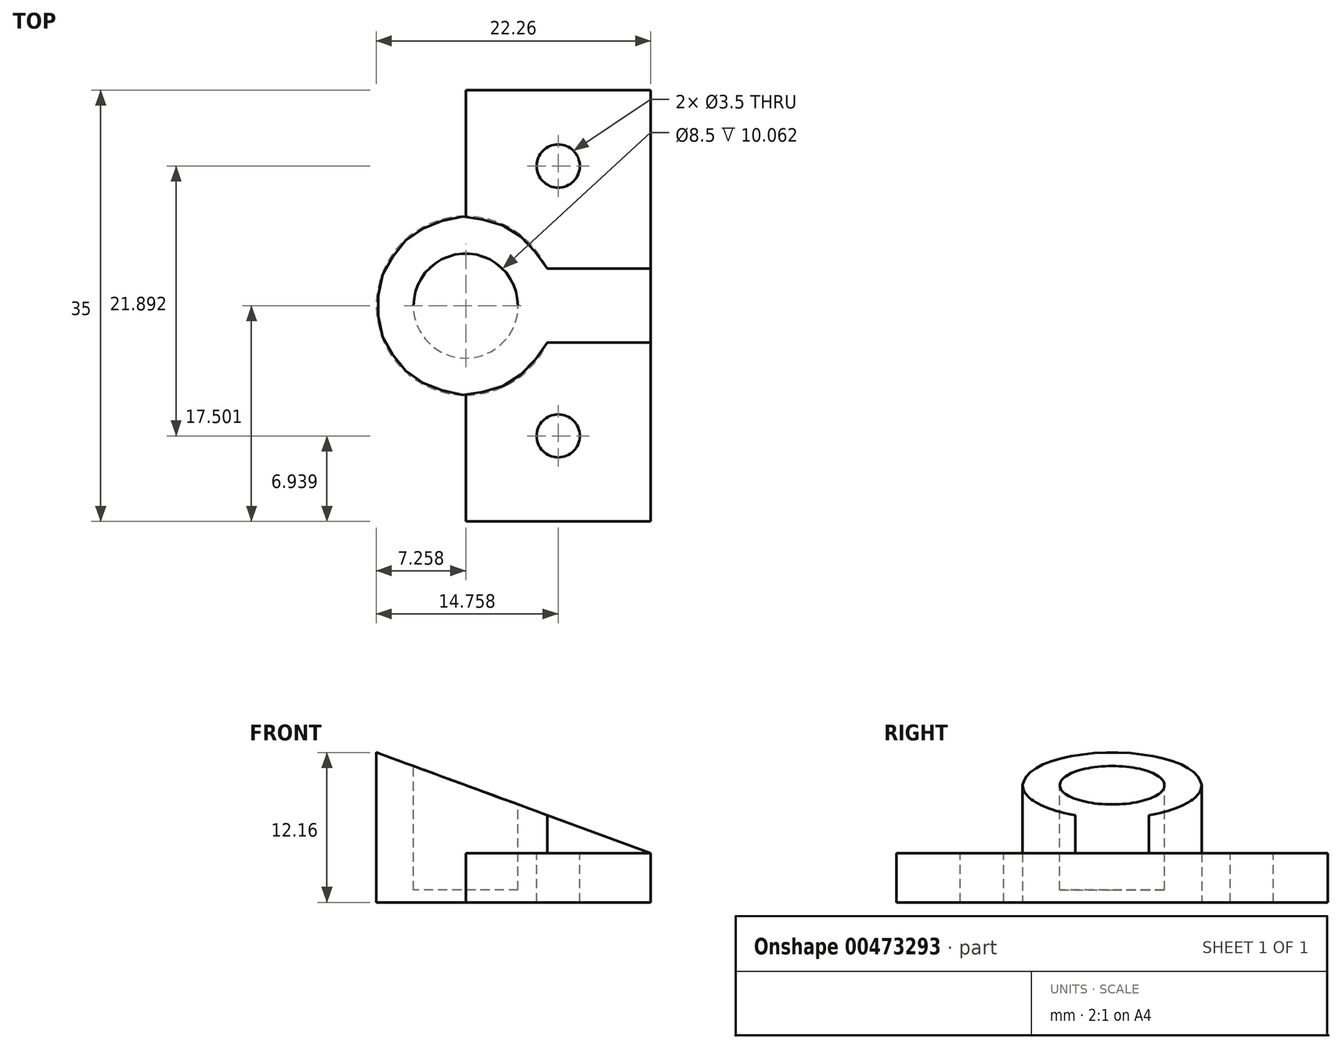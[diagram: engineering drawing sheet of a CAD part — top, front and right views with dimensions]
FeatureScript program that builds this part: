
annotation { "Feature Type Name" : "Feature", "Feature Type Description" : "" }
export const myFeature = defineFeature(function(context is Context, id is Id, definition is map)
    precondition{}
    {
        {
            var Q0;
            Q0=qCreatedBy(makeId("Top.planeOp"),FACE);
            var sketch = newSketch(context, id + "F0", { "sketchPlane" : qUnion([Q0])});
            skLineSegment(sketch, "E0.bottom", {"start": v(15.73, -2.25) * mm, "end": v(0.73, -2.25) * mm});
            skLineSegment(sketch, "E0.top", {"start": v(15.73, 32.75) * mm, "end": v(0.73, 32.75) * mm});
            skLineSegment(sketch, "E0.left", {"start": v(15.73, -2.25) * mm, "end": v(15.73, 32.75) * mm});
            skLineSegment(sketch, "E0.right", {"start": v(0.73, -2.25) * mm, "end": v(0.73, 32.75) * mm});
            skSolve(sketch);
        }
        {
            var Q0;
            Q0=qSketchRegion(id+"F0",true);
            extrude(context, id + "F1", {"entities" : qUnion([Q0]), "depth" : 4 * mm, "offsetDistance" : 25 * mm});
        }
        {
            var Q0;
            Q0=makeQuery(id+"F1.opExtrude","SWEPT_FACE",FACE,{"disambiguationData":[OSD([sQuery(id+"F0.wireOp",EDGE,"E0.top")])]});
            var sketch = newSketch(context, id + "F2", { "sketchPlane" : qUnion([Q0])});
            skArc(sketch, "E1", {"start": v(23.96, 8.4) * mm, "mid": v(24.64, 14.63) * mm, "end": v(18.7, 16.63) * mm});
            skCircle(sketch, "E2", {"center": v(20.42, 11.94) * mm, "radius": 1.75 * mm});
            skLineSegment(sketch, "E3", {"start": v(23.96, 8.4) * mm, "end": v(15.56, 0) * mm});
            skLineSegment(sketch, "E4", {"start": v(-0.73, 0) * mm, "end": v(15.56, 0) * mm});
            skLineSegment(sketch, "E5", {"start": v(-15.73, 4) * mm, "end": v(-0.73, 4) * mm});
            skLineSegment(sketch, "E6", {"start": v(-0.73, 4) * mm, "end": v(-0.73, 0) * mm});
            skLineSegment(sketch, "E7", {"start": v(-15.73, 4) * mm, "end": v(18.7, 16.63) * mm});
            skSolve(sketch);
        }
        {
            var Q0;
            Q0=qSketchRegion(id+"F2",true);
            extrude(context, id + "F3", {"entities" : qUnion([Q0]), "operationType" : NewBodyOperationType.ADD, "oppositeDirection" : true, "depth" : 35 * mm, "offsetDistance" : 25 * mm});
        }
        {
            var Q0;
            Q0=makeQuery(id+"F1.opExtrude","SWEPT_FACE",FACE,{"disambiguationData":[OSD([sQuery(id+"F0.wireOp",EDGE,"E0.left")])]});
            var sketch = newSketch(context, id + "F4", { "sketchPlane" : qUnion([Q0])});
            skLineSegment(sketch, "E8.bottom", {"start": v(3.25, 4) * mm, "end": v(12.25, 4) * mm});
            skLineSegment(sketch, "E8.top", {"start": v(3.25, 18.37) * mm, "end": v(12.25, 18.37) * mm});
            skLineSegment(sketch, "E8.left", {"start": v(3.25, 4) * mm, "end": v(3.25, 18.37) * mm});
            skLineSegment(sketch, "E8.right", {"start": v(12.25, 4) * mm, "end": v(12.25, 18.37) * mm});
            skLineSegment(sketch, "E9.bottom", {"start": v(18.25, 4) * mm, "end": v(27.25, 4) * mm});
            skLineSegment(sketch, "E9.top", {"start": v(18.25, 18.22) * mm, "end": v(27.25, 18.22) * mm});
            skLineSegment(sketch, "E9.left", {"start": v(18.25, 4) * mm, "end": v(18.25, 18.22) * mm});
            skLineSegment(sketch, "E9.right", {"start": v(27.25, 4) * mm, "end": v(27.25, 18.22) * mm});
            skSolve(sketch);
        }
        {
            var Q0;
            Q0=qSketchRegion(id+"F4",true);
            extrude(context, id + "F5", {"entities" : qUnion([Q0]), "operationType" : NewBodyOperationType.REMOVE, "oppositeDirection" : true, "depth" : 47.1 * mm, "offsetDistance" : 25 * mm});
        }
        {
            var Q0;
            Q0=makeQuery(id+"F5.boolean.opBoolean","COPY",FACE,{"derivedFrom":makeQuery(id+"F5.opExtrude","SWEPT_FACE",FACE,{"disambiguationData":[OSD([sQuery(id+"F4.wireOp",EDGE,"E9.bottom")])]})});
            var sketch = newSketch(context, id + "F6", { "sketchPlane" : qUnion([Q0])});
            skPoint(sketch, "E10.0", {"position": v(15.73, 15.25) * mm});
            skCircle(sketch, "E11", {"center": v(0.73, 15.25) * mm, "radius": 4.25 * mm});
            skCircle(sketch, "E12", {"center": v(0.73, 15.25) * mm, "radius": 8 * mm, "construction": true});
            skSolve(sketch);
        }
        {
            var Q0;
            Q0=qSketchRegion(id+"F6",true);
            extrude(context, id + "F7", {"entities" : qUnion([Q0]), "operationType" : NewBodyOperationType.REMOVE, "oppositeDirection" : true, "depth" : 3 * mm, "offsetDistance" : 25 * mm, "hasSecondDirection" : true, "secondDirectionOppositeDirection" : false, "secondDirectionDepth" : 83.2 * mm});
        }
        {
            var Q0;
            Q0=makeQuery(id+"F5.boolean.opBoolean","COPY",FACE,{"derivedFrom":makeQuery(id+"F5.opExtrude","SWEPT_FACE",FACE,{"disambiguationData":[OSD([sQuery(id+"F4.wireOp",EDGE,"E9.bottom")])]})});
            var sketch = newSketch(context, id + "F8", { "sketchPlane" : qUnion([Q0])});
            skCircle(sketch, "E13", {"center": v(0.73, 15.25) * mm, "radius": 7.26 * mm});
            skArc(sketch, "E14.0", {"start": v(-2.28, 18.25) * mm, "mid": v(0.73, 19.5) * mm, "end": v(3.74, 18.25) * mm});
            skCircle(sketch, "E15.0.0", {"center": v(0.73, 15.25) * mm, "radius": 4.25 * mm});
            skSolve(sketch);
        }
        {
            var Q0;
            Q0=qSketchRegion(id+"F8",true);
            var Q1;
            {var subQ0=makeQuery(id+"F3.opExtrude","SWEPT_FACE",FACE,{"disambiguationData":[OSD([sQuery(id+"F2.wireOp",EDGE,"E1")])]});var subQ1=makeQuery(id+"F5.opExtrude","SWEPT_FACE",FACE,{"disambiguationData":[OSD([sQuery(id+"F4.wireOp",EDGE,"E8.right")])]});Q1=makeQuery(id+"F7.boolean.opBoolean","SPLIT",FACE,{"disambiguationData":[TD([subQ0])],"derivedFrom":makeQuery(id+"F5.boolean.opBoolean","SPLIT",FACE,{"disambiguationData":[TD([subQ1])],"derivedFrom":makeQuery(id+"F3.opExtrude","SWEPT_FACE",FACE,{"disambiguationData":[OSD([sQuery(id+"F2.wireOp",EDGE,"E7")])]})})});}
            extrude(context, id + "F9", {"entities" : qUnion([Q0]), "operationType" : NewBodyOperationType.ADD, "endBound" : BoundingType.UP_TO_SURFACE, "depth" : 25 * mm, "endBoundEntityFace" : qUnion([Q1]), "offsetDistance" : 25 * mm});
        }
        {
            var Q0;
            Q0=makeQuery(id+"F3.boolean.opBoolean","MERGE",FACE,{"derivedFrom":[makeQuery(id+"F1.opExtrude","CAP_FACE",FACE,{"disambiguationData":[OSD([sQuery(id+"F0.wireOp",EDGE,"E0.bottom"),sQuery(id+"F0.wireOp",EDGE,"E0.top"),sQuery(id+"F0.wireOp",EDGE,"E0.left"),sQuery(id+"F0.wireOp",EDGE,"E0.right")])],"isStart":true}),makeQuery(id+"F3.opExtrude","SWEPT_FACE",FACE,{"disambiguationData":[OSD([sQuery(id+"F2.wireOp",EDGE,"E4")])]})]});
            var sketch = newSketch(context, id + "F10", { "sketchPlane" : qUnion([Q0])});
            skPoint(sketch, "E16", {"position": v(0.73, 2.25) * mm});
            skLineSegment(sketch, "E17.0", {"start": v(-19.56, -3.25) * mm, "end": v(-19.56, -12.25) * mm});
            skLineSegment(sketch, "E18.0", {"start": v(-19.56, -18.25) * mm, "end": v(-19.56, -27.25) * mm});
            skLineSegment(sketch, "E19.bottom", {"start": v(-19.56, -3.25) * mm, "end": v(0.73, -3.25) * mm});
            skLineSegment(sketch, "E19.top", {"start": v(-19.56, -12.25) * mm, "end": v(-5.88, -12.25) * mm});
            skLineSegment(sketch, "E19.right", {"start": v(0.73, -3.25) * mm, "end": v(0.73, -8) * mm});
            skLineSegment(sketch, "E20.bottom", {"start": v(-19.56, -18.25) * mm, "end": v(-5.88, -18.25) * mm});
            skLineSegment(sketch, "E20.top", {"start": v(-19.56, -27.25) * mm, "end": v(0.73, -27.25) * mm});
            skLineSegment(sketch, "E20.right", {"start": v(0.73, -22.5) * mm, "end": v(0.73, -27.25) * mm});
            skArc(sketch, "E21.0", {"start": v(0.73, -22.5) * mm, "mid": v(-3.2, -21.35) * mm, "end": v(-5.88, -18.25) * mm});
            skArc(sketch, "E22.0", {"start": v(-5.88, -12.25) * mm, "mid": v(-3.2, -9.15) * mm, "end": v(0.73, -8) * mm});
            skPoint(sketch, "E23.orphan", {"position": v(7.34, -18.25) * mm});
            skPoint(sketch, "E24.orphan", {"position": v(0.73, -12.25) * mm});
            skPoint(sketch, "E25.orphan", {"position": v(7.34, -12.25) * mm});
            skSolve(sketch);
        }
        {
            var Q0;
            Q0=qSketchRegion(id+"F10",true);
            extrude(context, id + "F11", {"entities" : qUnion([Q0]), "operationType" : NewBodyOperationType.REMOVE, "oppositeDirection" : true, "depth" : 25 * mm, "offsetDistance" : 25 * mm});
        }
        {
            var Q0;
            Q0=makeQuery(id+"F5.boolean.opBoolean","COPY",FACE,{"derivedFrom":makeQuery(id+"F5.opExtrude","SWEPT_FACE",FACE,{"disambiguationData":[OSD([sQuery(id+"F4.wireOp",EDGE,"E8.bottom")])]})});
            var sketch = newSketch(context, id + "F12", { "sketchPlane" : qUnion([Q0])});
            skCircle(sketch, "E26", {"center": v(8.23, 4.69) * mm, "radius": 1.75 * mm});
            skPoint(sketch, "E26.centerSnap0", {"position": v(15.73, 7.75) * mm});
            skPoint(sketch, "E26.centerSnap1", {"position": v(8.23, 3.25) * mm});
            skPoint(sketch, "E27.0", {"position": v(15.73, 22.75) * mm});
            skCircle(sketch, "E28", {"center": v(8.23, 26.58) * mm, "radius": 1.75 * mm});
            skSolve(sketch);
        }
        {
            var Q0;
            Q0=qSketchRegion(id+"F12",true);
            extrude(context, id + "F13", {"entities" : qUnion([Q0]), "operationType" : NewBodyOperationType.REMOVE, "oppositeDirection" : true, "depth" : 25 * mm, "offsetDistance" : 25 * mm});
        }
        {
            var Q0;
            Q0=makeQuery(id+"F11.boolean.opBoolean","MERGE",FACE,{"derivedFrom":[makeQuery(id+"F5.boolean.opBoolean","COPY",FACE,{"derivedFrom":makeQuery(id+"F5.opExtrude","SWEPT_FACE",FACE,{"disambiguationData":[OSD([sQuery(id+"F4.wireOp",EDGE,"E9.right")])]})})],"fromTools":[makeQuery(id+"F11.opExtrude","SWEPT_FACE",FACE,{"disambiguationData":[OSD([sQuery(id+"F10.wireOp",EDGE,"E20.top")])]})]});
            extrude(context, id + "F14", {"entities" : qUnion([Q0]), "operationType" : NewBodyOperationType.REMOVE, "oppositeDirection" : true, "depth" : 25 * mm, "offsetDistance" : 25 * mm});
        }
        {
            var Q0;
            Q0=makeQuery(id+"F11.boolean.opBoolean","MERGE",FACE,{"derivedFrom":[makeQuery(id+"F5.boolean.opBoolean","COPY",FACE,{"derivedFrom":makeQuery(id+"F5.opExtrude","SWEPT_FACE",FACE,{"disambiguationData":[OSD([sQuery(id+"F4.wireOp",EDGE,"E8.left")])]})})],"fromTools":[makeQuery(id+"F11.opExtrude","SWEPT_FACE",FACE,{"disambiguationData":[OSD([sQuery(id+"F10.wireOp",EDGE,"E19.bottom")])]})]});
            extrude(context, id + "F15", {"entities" : qUnion([Q0]), "operationType" : NewBodyOperationType.REMOVE, "oppositeDirection" : true, "depth" : 25 * mm, "offsetDistance" : 25 * mm});
        }
        {
            var Q0;
            Q0=makeQuery(id+"F11.boolean.opBoolean","MERGE",FACE,{"derivedFrom":[makeQuery(id+"F7.boolean.opBoolean","SPLIT",FACE,{"disambiguationData":[TD([makeQuery(id+"F3.opExtrude","SWEPT_FACE",FACE,{"disambiguationData":[OSD([sQuery(id+"F2.wireOp",EDGE,"E1")])]})])],"derivedFrom":makeQuery(id+"F5.boolean.opBoolean","COPY",FACE,{"derivedFrom":makeQuery(id+"F5.opExtrude","SWEPT_FACE",FACE,{"disambiguationData":[OSD([sQuery(id+"F4.wireOp",EDGE,"E8.right")])]})})})],"fromTools":[makeQuery(id+"F11.opExtrude","SWEPT_FACE",FACE,{"disambiguationData":[OSD([sQuery(id+"F10.wireOp",EDGE,"E19.top")])]})]});
            extrude(context, id + "F16", {"entities" : qUnion([Q0]), "operationType" : NewBodyOperationType.REMOVE, "oppositeDirection" : true, "depth" : 25 * mm, "offsetDistance" : 25 * mm});
        }
        {
            var Q0;
            Q0=makeQuery(id+"F3.boolean.opBoolean","MERGE",FACE,{"derivedFrom":[makeQuery(id+"F1.opExtrude","CAP_FACE",FACE,{"disambiguationData":[OSD([sQuery(id+"F0.wireOp",EDGE,"E0.bottom"),sQuery(id+"F0.wireOp",EDGE,"E0.top"),sQuery(id+"F0.wireOp",EDGE,"E0.left"),sQuery(id+"F0.wireOp",EDGE,"E0.right")])],"isStart":true}),makeQuery(id+"F3.opExtrude","SWEPT_FACE",FACE,{"disambiguationData":[OSD([sQuery(id+"F2.wireOp",EDGE,"E4")])]})]});
            var sketch = newSketch(context, id + "F17", { "sketchPlane" : qUnion([Q0])});
            skArc(sketch, "E29", {"start": v(-5.88, -12.25) * mm, "mid": v(-6.53, -15.25) * mm, "end": v(-5.88, -18.25) * mm});
            skLineSegment(sketch, "E30", {"start": v(-5.88, -12.25) * mm, "end": v(-5.88, -18.25) * mm});
            skSolve(sketch);
        }
        {
            var Q0;
            Q0 = qSketchRegion(id + "F17", true);
            var Q1;
            {var subQ1=makeQuery(id+"F5.opExtrude","SWEPT_FACE",FACE,{"disambiguationData":[OSD([sQuery(id+"F4.wireOp",EDGE,"E8.right")])]});var subQ4=makeQuery(id+"F1.opExtrude","SWEPT_FACE",FACE,{"disambiguationData":[OSD([sQuery(id+"F0.wireOp",EDGE,"E0.left")])]});var subQ8=makeQuery(id+"F3.opExtrude","SWEPT_FACE",FACE,{"disambiguationData":[OSD([sQuery(id+"F2.wireOp",EDGE,"E1")])]});var subQ9=makeQuery(id+"F5.boolean.opBoolean","SPLIT",FACE,{"disambiguationData":[TD([subQ1])],"derivedFrom":makeQuery(id+"F3.opExtrude","SWEPT_FACE",FACE,{"disambiguationData":[OSD([sQuery(id+"F2.wireOp",EDGE,"E7")])]})});Q1=makeQuery(id+"F9.boolean.opBoolean","MERGE",FACE,{"derivedFrom":[makeQuery(id+"F7.boolean.opBoolean","SPLIT",FACE,{"disambiguationData":[TD([subQ8])],"derivedFrom":subQ9}),makeQuery(id+"F7.boolean.opBoolean","SPLIT",FACE,{"disambiguationData":[TD([subQ4])],"derivedFrom":subQ9}),makeQuery(id+"F9.opExtrude","CAP_FACE",FACE,{"disambiguationData":[OSD([sQuery(id+"F8.wireOp",EDGE,"E13"),sQuery(id+"F8.wireOp",EDGE,"E15.0.0")])],"isStart":false})]});}
            extrude(context, id + "F18", {"entities" : qUnion([Q0]), "operationType" : NewBodyOperationType.ADD, "endBound" : BoundingType.UP_TO_SURFACE, "oppositeDirection" : true, "depth" : 25 * mm, "endBoundEntityFace" : qUnion([Q1]), "offsetDistance" : 25 * mm});
        }
    });
